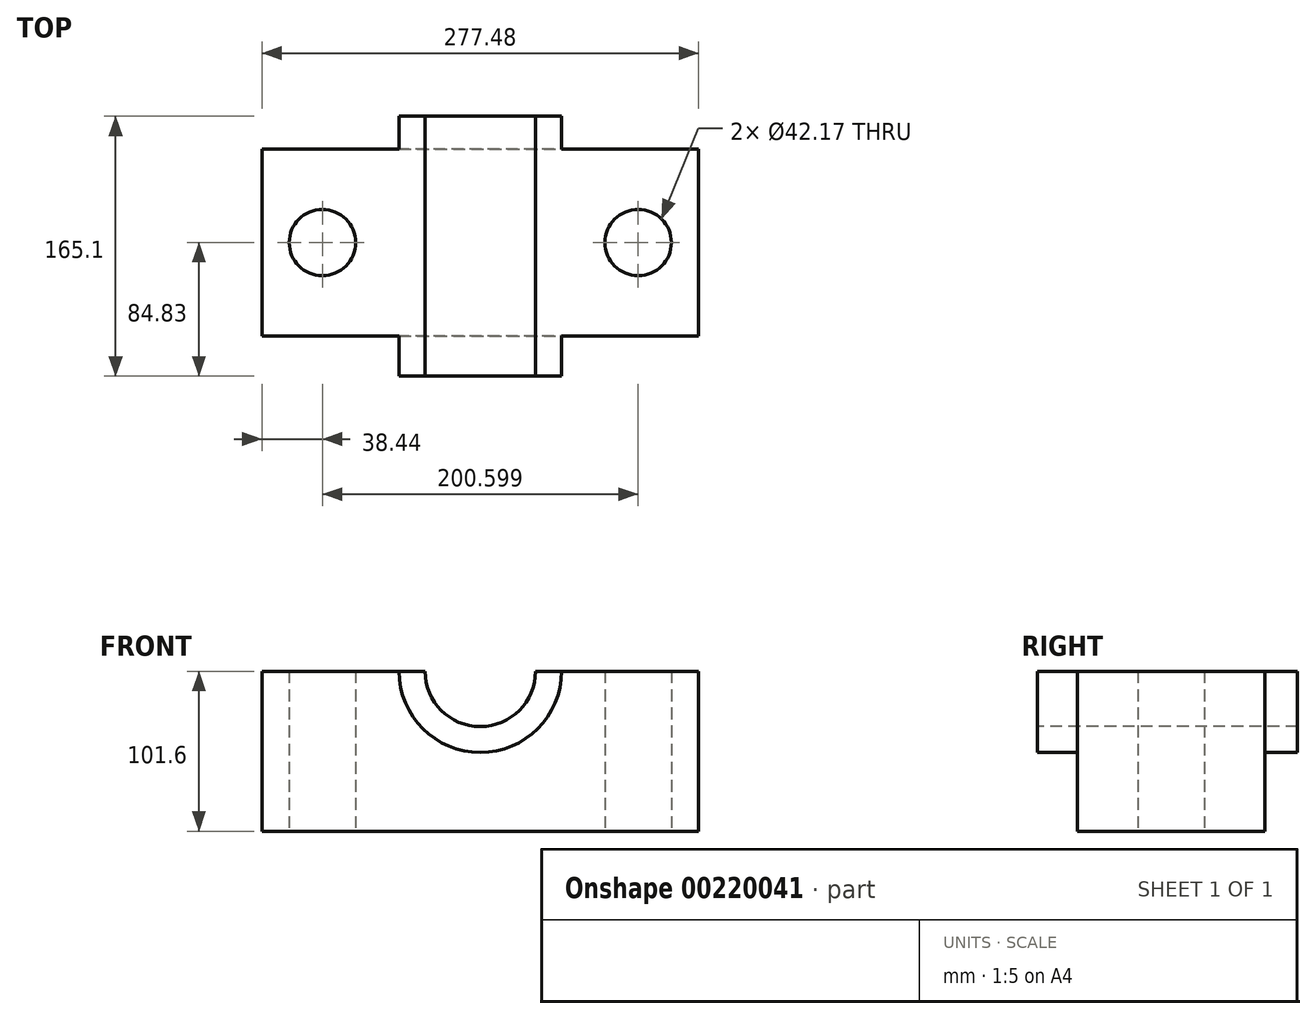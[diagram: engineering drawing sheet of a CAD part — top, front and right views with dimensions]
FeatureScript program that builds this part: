
annotation { "Feature Type Name" : "Feature", "Feature Type Description" : "" }
export const myFeature = defineFeature(function(context is Context, id is Id, definition is map)
    precondition{}
    {
        {
            var Q0;
            Q0=qCreatedBy(makeId("Top.planeOp"),FACE);
            var sketch = newSketch(context, id + "F0", { "sketchPlane" : qUnion([Q0])});
            skLineSegment(sketch, "E0.bottom", {"start": v(138.74, 59.43) * mm, "end": v(-138.74, 59.43) * mm});
            skLineSegment(sketch, "E0.top", {"start": v(138.74, -59.43) * mm, "end": v(-138.74, -59.43) * mm});
            skLineSegment(sketch, "E0.left", {"start": v(138.74, 59.43) * mm, "end": v(138.74, -59.43) * mm});
            skLineSegment(sketch, "E0.right", {"start": v(-138.74, 59.43) * mm, "end": v(-138.74, -59.43) * mm});
            skPoint(sketch, "E0.middle", {"position": v(0, 0) * mm});
            skCircle(sketch, "E1", {"center": v(-100.3, 0) * mm, "radius": 21.09 * mm});
            skCircle(sketch, "E2.MirrorC", {"center": v(100.3, 0) * mm, "radius": 21.09 * mm});
            skSolve(sketch);
        }
        {
            var Q0;
            Q0 = qSketchRegion(id + "F0", true);
            extrude(context, id + "F1", {"entities" : qUnion([Q0]), "depth" : 101.6 * mm});
        }
        {
            var Q0;
            Q0=makeQuery(id+"F1.opExtrude","SWEPT_FACE",FACE,{"disambiguationData":[OSD([sQuery(id+"F0.wireOp",EDGE,"E0.top")])]});
            var sketch = newSketch(context, id + "F2", { "sketchPlane" : qUnion([Q0])});
            skCircle(sketch, "E3", {"center": v(0, 101.6) * mm, "radius": 35.08 * mm});
            skSolve(sketch);
        }
        {
            var Q0;
            Q0 = qSketchRegion(id + "F2", true);
            extrude(context, id + "F3", {"entities" : qUnion([Q0]), "operationType" : NewBodyOperationType.REMOVE, "endBound" : BoundingType.THROUGH_ALL, "oppositeDirection" : true, "depth" : 25.4 * mm});
        }
        {
            var Q0;
            Q0=makeQuery(id+"F1.opExtrude","SWEPT_FACE",FACE,{"disambiguationData":[OSD([sQuery(id+"F0.wireOp",EDGE,"E0.top")])]});
            var sketch = newSketch(context, id + "F4", { "sketchPlane" : qUnion([Q0])});
            skArc(sketch, "E4.0", {"start": v(-35.08, 101.6) * mm, "mid": v(0, 66.52) * mm, "end": v(35.08, 101.6) * mm});
            skLineSegment(sketch, "E5.0", {"start": v(138.74, 101.6) * mm, "end": v(35.08, 101.6) * mm});
            skLineSegment(sketch, "E6.0", {"start": v(-35.08, 101.6) * mm, "end": v(-138.74, 101.6) * mm});
            skLineSegment(sketch, "E7.0", {"start": v(138.74, 0) * mm, "end": v(-138.74, 0) * mm});
            skLineSegment(sketch, "E8.0", {"start": v(138.74, 101.6) * mm, "end": v(138.74, 0) * mm});
            skLineSegment(sketch, "E9.0", {"start": v(-138.74, 101.6) * mm, "end": v(-138.74, 0) * mm});
            skArc(sketch, "E10", {"start": v(-51.58, 101.6) * mm, "mid": v(0, 50.02) * mm, "end": v(51.58, 101.6) * mm});
            skSolve(sketch);
        }
        {
            var Q0;
            {var subQ0=sQuery(id+"F4.wireOp",EDGE,"E4.0");Q0=makeQuery(id+"F4.imprint","IMPRINT",FACE,{"disambiguationData":[TD([[makeQuery(id+"F4.imprint","IMPRINT",EDGE,{"derivedFrom":subQ0}),-1.0]])]});}
            extrude(context, id + "F5", {"entities" : qUnion([Q0]), "operationType" : NewBodyOperationType.ADD, "depth" : 25.4 * mm, "hasSecondDirection" : true, "secondDirectionOppositeDirection" : true, "secondDirectionDepth" : 139.7 * mm});
        }
    });
